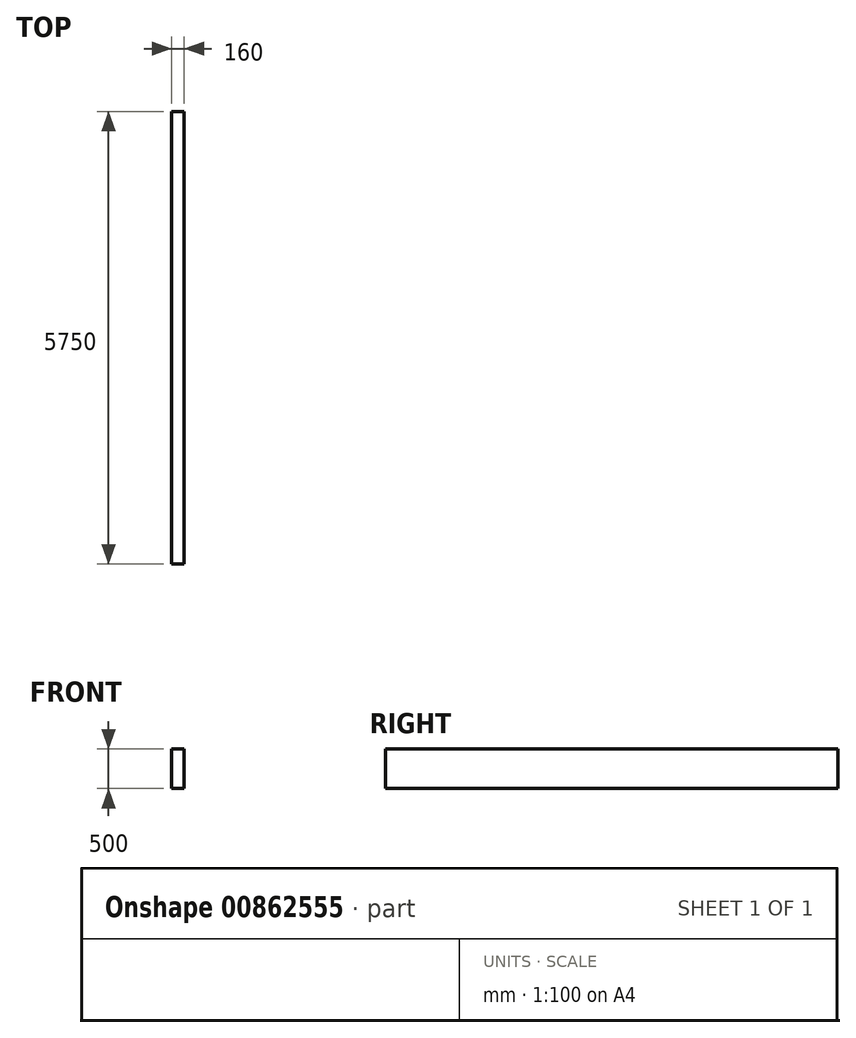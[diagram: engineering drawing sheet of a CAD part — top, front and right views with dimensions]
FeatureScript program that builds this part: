
annotation { "Feature Type Name" : "Feature", "Feature Type Description" : "" }
export const myFeature = defineFeature(function(context is Context, id is Id, definition is map)
    precondition{}
    {
        {
            var Q0;
            Q0=qCreatedBy(makeId("Front.planeOp"),FACE);
            var sketch = newSketch(context, id + "F0", { "sketchPlane" : qUnion([Q0])});
            skLineSegment(sketch, "E0.bottom", {"start": v(0, 0) * mm, "end": v(160, 0) * mm});
            skLineSegment(sketch, "E0.top", {"start": v(0, -500) * mm, "end": v(160, -500) * mm});
            skLineSegment(sketch, "E0.left", {"start": v(0, 0) * mm, "end": v(0, -500) * mm});
            skLineSegment(sketch, "E0.right", {"start": v(160, 0) * mm, "end": v(160, -500) * mm});
            skSolve(sketch);
        }
        {
            var Q0;
            Q0=makeQuery(id+"F0.imprint","IMPRINT",FACE,{"disambiguationData":[TD([[makeQuery(id+"F0.imprint","IMPRINT",EDGE,{"derivedFrom":sQuery(id+"F0.wireOp",EDGE,"E0.bottom")}),-1.0]])]});
            extrude(context, id + "F1", {"entities" : qUnion([Q0]), "depth" : 5750 * mm, "offsetDistance" : 25 * mm});
        }
    });
